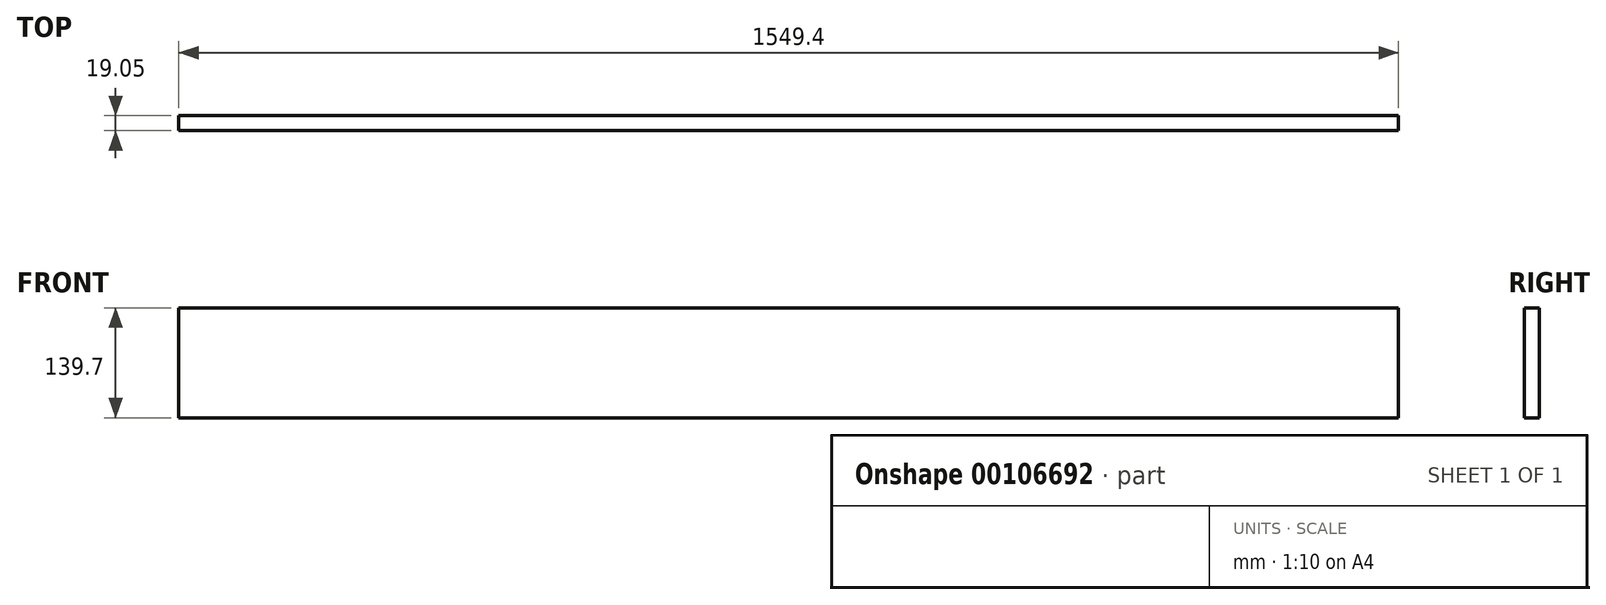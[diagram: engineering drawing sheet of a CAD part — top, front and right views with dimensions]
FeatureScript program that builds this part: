
annotation { "Feature Type Name" : "Feature", "Feature Type Description" : "" }
export const myFeature = defineFeature(function(context is Context, id is Id, definition is map)
    precondition{}
    {
        {
            var Q0;
            Q0=qCreatedBy(makeId("Front.planeOp"),FACE);
            var sketch = newSketch(context, id + "F0", { "sketchPlane" : qUnion([Q0])});
            skLineSegment(sketch, "E0.bottom", {"start": v(0, 0) * mm, "end": v(1549.4, 0) * mm});
            skLineSegment(sketch, "E0.top", {"start": v(0, 139.7) * mm, "end": v(1549.4, 139.7) * mm});
            skLineSegment(sketch, "E0.left", {"start": v(0, 0) * mm, "end": v(0, 139.7) * mm});
            skLineSegment(sketch, "E0.right", {"start": v(1549.4, 0) * mm, "end": v(1549.4, 139.7) * mm});
            skSolve(sketch);
        }
        {
            var Q0;
            Q0=makeQuery(id+"F0.imprint","IMPRINT",FACE,{"disambiguationData":[TD([[makeQuery(id+"F0.imprint","IMPRINT",EDGE,{"derivedFrom":sQuery(id+"F0.wireOp",EDGE,"E0.bottom")}),1.0]])]});
            extrude(context, id + "F1", {"entities" : qUnion([Q0]), "depth" : 19.05 * mm});
        }
    });
